# Revit family: P2669-12930K
name_source: partatom
category: Lighting Fixtures
revit_build: Autodesk Revit 2014 (Build: 20130308_1515(x64)
units: mm (PartAtom-declared; Revit-internal decimal feet)

## types (1)
- P2669-12930K
    Apparent Load = 24 VA
    Assembly Code = D5020200
    Color Filter = 16777215
    Connector Description = Lighting Connector
    Default Elevation = 48"
    Description = Frosted polycarbonate shade
• Coated in an architectural bronze finish.
• Ideal for ceiling fans mounted in a great room, bedroom, living room, or bonus room.
• Includes LED light source.
• Frosted shatterproof shade.
• 83 lum/watt with 3000K.
• Measures 6-7/8-inch width by 2-7/8-inch height.
• Dry location listed.
• 5-year limited warranty.
• Includes installation instructions and mounting hardware.
• Progress Lighting products are designed for exceptional quality, reliability, and functionality.
• Dimmable to 10% brightness (See Dimming Notes)
    Diameter = 6 15/16"
    Dimming Lamp Color Temperature Shift = <None>
    Emit Shape Visible in Rendering = No
    Emit from Circle Diameter = 6 15/16"
    Features = White PMMA diffuser
• Features a crisp white shade shaped into a bowl silhouette.
• Stylishly simple design with a seamless aesthetic.
• Perfect for any modern, luxury, or transitional setting.
• Damp location listed.
• 5-Year Limited Warranty.
• Measures 11-inch width by 3-1/2-inch height.
• Uses one integrated LED (14.5w).
• Includes installation instructions and mounting hardware.
• Progress Lighting products are designed for exceptional quality, reliability, and functionality.
• Dimmable to 10% brightness (See Dimming Notes)
• Fixture covers a standard 4” recessed outlet box
• Mounting backplate for outlet box included
• 6 in of wire supplied
    Fixture distribution = Direct
    Glass = Hubbell - Glass
    Height = 1 1/2"
    Housing Material = Paint - Hubbell - Textured Camera Black
    Lamp = LED
    Load Classification = Lighting
    Manufacturer = Progress Lighting
    Model = P2669-12930K
    Photometric Web File = generic.ies
    Power Factor = 1
    Product Documentation Link = https://hubbellcdn.com
    Product Link = https://www.hubbell.com
    Tilt Angle = -90.00°
    URL = https://www.hubbell.com
    Voltage = 120 V
    Warranty = 5 years Warranty
    Wattage Comments = 24W
    Watts = 24 W

## geometry (parser evidence)
native form markers: Sweep x4
no freeform markers — native parametric forms only
